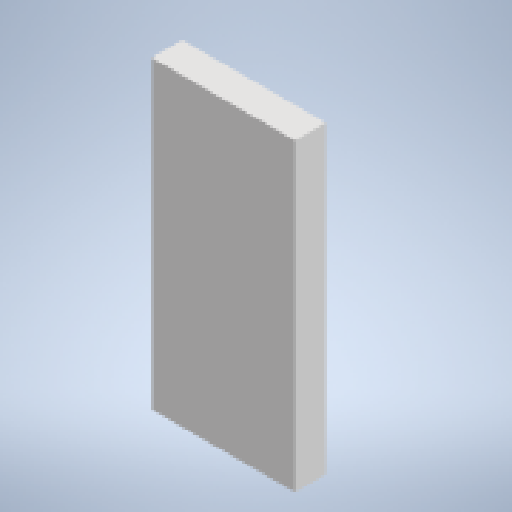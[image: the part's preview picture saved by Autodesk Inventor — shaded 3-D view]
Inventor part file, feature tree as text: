
AUTODESK INVENTOR PART (.ipt)
format: ipt  version: 2024 (Build 280153000, 153)  size: 138,240 bytes
history: native  units: in
note: dims shown in document units (in); Inventor stores cm internally (conversion verified against a paired STEP export)
features: extrude x2, sketch x1
ambient origin geometry x8: Origin, YZ Plane, XZ Plane, XY Plane, X Axis, Y Axis, Z Axis, Center Point
bodies: Solid1 (feature_tree)
feature tree (3):
  sketch  "Sketch1"  dims[d0=0.3031in d2=0.063in d3=0.063in d4=0.0669in d5=0.0669in d6=0.0315in d7=0.0in d8=0.0354in d9=0.0in d10=0.0561in d11=0.0118in]
  extrude  "Extrusion1"  Depth=0.063in
  extrude  "Extrusion2"  Depth=0.063in
